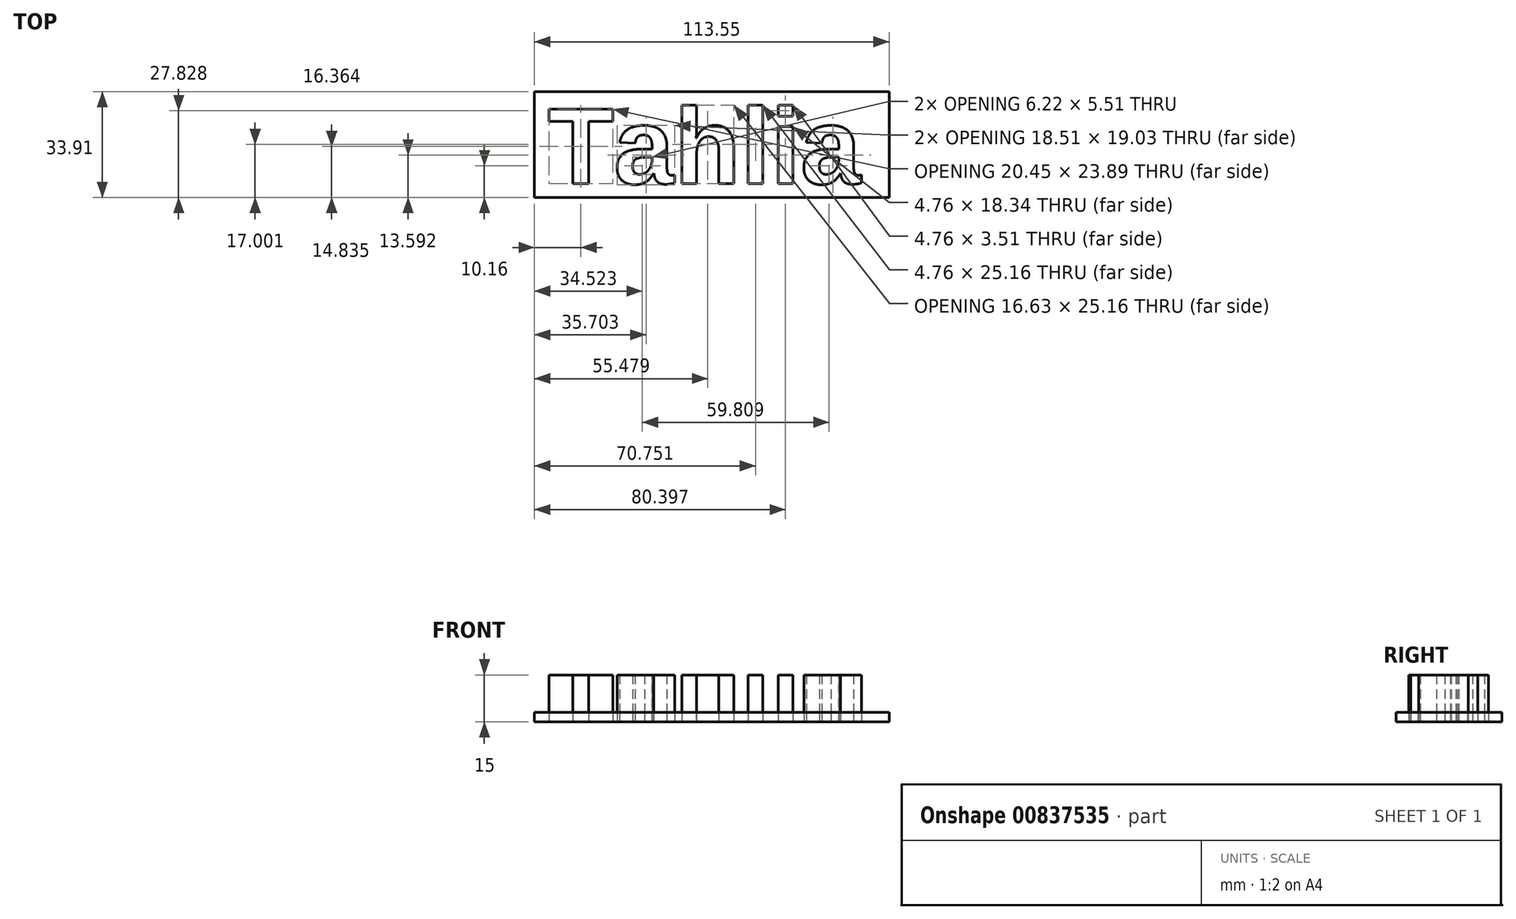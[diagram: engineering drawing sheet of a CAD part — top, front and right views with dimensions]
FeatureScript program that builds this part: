
annotation { "Feature Type Name" : "Feature", "Feature Type Description" : "" }
export const myFeature = defineFeature(function(context is Context, id is Id, definition is map)
    precondition{}
    {
        {
            var Q0;
            Q0=qCreatedBy(makeId("Top.planeOp"),FACE);
            var sketch = newSketch(context, id + "F0", { "sketchPlane" : qUnion([Q0])});
            skLineSegment(sketch, "E0.bottom", {"start": v(-59.56, -10.9) * mm, "end": v(53.99, -10.9) * mm});
            skLineSegment(sketch, "E0.top", {"start": v(-59.56, -44.8) * mm, "end": v(53.99, -44.8) * mm});
            skLineSegment(sketch, "E0.left", {"start": v(-59.56, -10.9) * mm, "end": v(-59.56, -44.8) * mm});
            skLineSegment(sketch, "E0.right", {"start": v(53.99, -10.9) * mm, "end": v(53.99, -44.8) * mm});
            skText(sketch, "E1", { "text": "Tahlia", "fontName": "Arimo-Bold.ttf"});
            skPoint(sketch, "E2", {"position": v(-55.34, -27.89) * mm});
            skPoint(sketch, "E3", {"position": v(-59.56, -27.85) * mm});
            const initialGuessF0  = {"E1": [-0.05534, -0.04039, 1, 0, 0.025]};
            skSetInitialGuess(sketch, initialGuessF0);
            skSolve(sketch);
        }
        {
            var Q0;
            Q0 = qSketchRegion(id + "F0", true);
            extrude(context, id + "F1", {"entities" : qUnion([Q0]), "depth" : 3 * mm, "offsetDistance" : 25 * mm});
        }
        {
            var Q0;
            Q0=makeQuery(id+"F0.imprint","IMPRINT",FACE,{"disambiguationData":[TD([[makeQuery(id+"F0.imprint","IMPRINT",EDGE,{"derivedFrom":sQuery(id+"F0.wireOp",EDGE,"E1.sketch_text.stroke-75")}),-1.0]])]});
            var Q1;
            Q1=makeQuery(id+"F0.imprint","IMPRINT",FACE,{"disambiguationData":[TD([[makeQuery(id+"F0.imprint","IMPRINT",EDGE,{"derivedFrom":sQuery(id+"F0.wireOp",EDGE,"E1.sketch_text.stroke-71")}),-1.0]])]});
            var Q2;
            Q2=makeQuery(id+"F0.imprint","IMPRINT",FACE,{"disambiguationData":[TD([[makeQuery(id+"F0.imprint","IMPRINT",EDGE,{"derivedFrom":sQuery(id+"F0.wireOp",EDGE,"E1.sketch_text.stroke-67")}),-1.0]])]});
            var Q3;
            Q3=makeQuery(id+"F0.imprint","IMPRINT",FACE,{"disambiguationData":[TD([[makeQuery(id+"F0.imprint","IMPRINT",EDGE,{"derivedFrom":sQuery(id+"F0.wireOp",EDGE,"E1.sketch_text.stroke-63")}),-1.0]])]});
            var Q4;
            Q4=makeQuery(id+"F0.imprint","IMPRINT",FACE,{"disambiguationData":[TD([[makeQuery(id+"F0.imprint","IMPRINT",EDGE,{"derivedFrom":sQuery(id+"F0.wireOp",EDGE,"E1.sketch_text.stroke-46")}),-1.0]])]});
            var Q5;
            Q5=makeQuery(id+"F0.imprint","IMPRINT",FACE,{"disambiguationData":[TD([[makeQuery(id+"F0.imprint","IMPRINT",EDGE,{"derivedFrom":sQuery(id+"F0.wireOp",EDGE,"E1.sketch_text.stroke-8")}),-1.0]])]});
            var Q6;
            Q6=makeQuery(id+"F0.imprint","IMPRINT",FACE,{"disambiguationData":[TD([[makeQuery(id+"F0.imprint","IMPRINT",EDGE,{"derivedFrom":sQuery(id+"F0.wireOp",EDGE,"E1.sketch_text.stroke-0")}),-1.0]])]});
            extrude(context, id + "F2", {"entities" : qUnion([Q0, Q1, Q2, Q3, Q4, Q5, Q6]), "depth" : 15 * mm, "offsetDistance" : 25 * mm});
        }
        {
            var Q0;
            Q0=makeQuery(id+"F0.imprint","IMPRINT",FACE,{"disambiguationData":[TD([[makeQuery(id+"F0.imprint","IMPRINT",EDGE,{"derivedFrom":sQuery(id+"F0.wireOp",EDGE,"E1.sketch_text.stroke-36")}),1.0]])]});
            var Q1;
            Q1=makeQuery(id+"F0.imprint","IMPRINT",FACE,{"disambiguationData":[TD([[makeQuery(id+"F0.imprint","IMPRINT",EDGE,{"derivedFrom":sQuery(id+"F0.wireOp",EDGE,"E1.sketch_text.stroke-103")}),1.0]])]});
            extrude(context, id + "F3", {"entities" : qUnion([Q0, Q1]), "depth" : 3 * mm, "offsetDistance" : 25 * mm});
        }
    });
